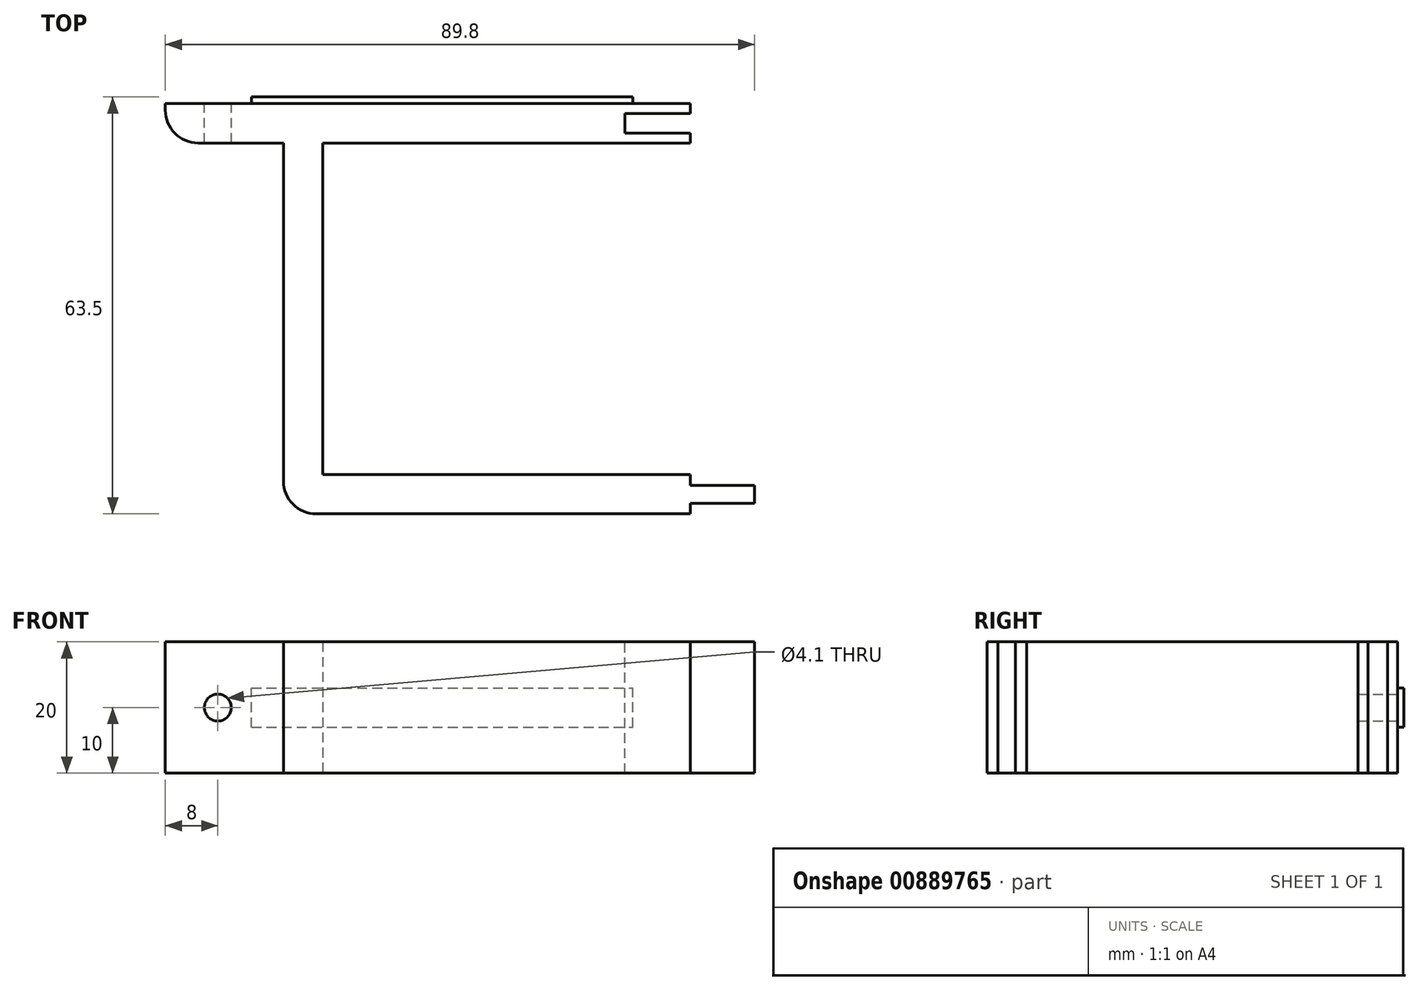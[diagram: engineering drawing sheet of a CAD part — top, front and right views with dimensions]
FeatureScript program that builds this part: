
annotation { "Feature Type Name" : "Feature", "Feature Type Description" : "" }
export const myFeature = defineFeature(function(context is Context, id is Id, definition is map)
    precondition{}
    {
        {
            var Q0;
            Q0=qCreatedBy(makeId("Top.planeOp"),FACE);
            var sketch = newSketch(context, id + "F0", { "sketchPlane" : qUnion([Q0])});
            skLineSegment(sketch, "E0.bottom", {"start": v(-80, 3) * mm, "end": v(80, 3) * mm});
            skLineSegment(sketch, "E0.top", {"start": v(-80, -3) * mm, "end": v(-62, -3) * mm});
            skLineSegment(sketch, "E0.left", {"start": v(-80, 3) * mm, "end": v(-80, -3) * mm});
            skLineSegment(sketch, "E0.right", {"start": v(80, 3) * mm, "end": v(80, -3) * mm});
            skPoint(sketch, "E0.middle", {"position": v(0, 0) * mm});
            skLineSegment(sketch, "E1.bottom", {"start": v(-56, -3) * mm, "end": v(56, -3) * mm});
            skLineSegment(sketch, "E1.top", {"start": v(-56, -53.5) * mm, "end": v(56, -53.5) * mm});
            skLineSegment(sketch, "E1.left", {"start": v(-56, -3) * mm, "end": v(-56, -53.5) * mm});
            skLineSegment(sketch, "E1.right", {"start": v(56, -3) * mm, "end": v(56, -53.5) * mm});
            skLineSegment(sketch, "E2", {"start": v(-62, -3) * mm, "end": v(-62, -59.5) * mm});
            skLineSegment(sketch, "E3", {"start": v(-62, -59.5) * mm, "end": v(62, -59.5) * mm});
            skLineSegment(sketch, "E4", {"start": v(62, -59.5) * mm, "end": v(62, -3) * mm});
            skLineSegment(sketch, "E5.trimOffspring", {"start": v(62, -3) * mm, "end": v(80, -3) * mm});
            skSolve(sketch);
        }
        {
            var Q0;
            Q0=makeQuery(id+"F0.imprint","IMPRINT",FACE,{"disambiguationData":[TD([[makeQuery(id+"F0.imprint","IMPRINT",EDGE,{"derivedFrom":sQuery(id+"F0.wireOp",EDGE,"E0.bottom")}),-1.0]])]});
            extrude(context, id + "F1", {"entities" : qUnion([Q0]), "depth" : 20 * mm, "offsetDistance" : 25 * mm});
        }
        {
            var Q0;
            Q0=makeQuery(id+"F1.opExtrude","SWEPT_EDGE",EDGE,{"disambiguationData":[OSD([sQuery(id+"F0.wireOp",EDGE,"E3"),sQuery(id+"F0.wireOp",EDGE,"E4")])]});
            var Q1;
            Q1=makeQuery(id+"F1.opExtrude","SWEPT_EDGE",EDGE,{"disambiguationData":[OSD([sQuery(id+"F0.wireOp",EDGE,"E2"),sQuery(id+"F0.wireOp",EDGE,"E3")])]});
            var Q2;
            Q2=makeQuery(id+"F1.opExtrude","SWEPT_EDGE",EDGE,{"disambiguationData":[OSD([sQuery(id+"F0.wireOp",EDGE,"E0.top"),sQuery(id+"F0.wireOp",EDGE,"E0.left")])]});
            var Q3;
            Q3=makeQuery(id+"F1.opExtrude","SWEPT_EDGE",EDGE,{"disambiguationData":[OSD([sQuery(id+"F0.wireOp",EDGE,"E0.right"),sQuery(id+"F0.wireOp",EDGE,"E5.trimOffspring")])]});
            fillet(context, id + "F2", {"entities" : qUnion([Q0, Q1, Q2, Q3]), "radius" : 5 * mm, "tangentPropagation" : true, "allowEdgeOverflow" : false});
        }
        {
            var Q0;
            Q0=makeQuery(id+"F1.opExtrude","SWEPT_FACE",FACE,{"disambiguationData":[OSD([sQuery(id+"F0.wireOp",EDGE,"E0.bottom")])]});
            var sketch = newSketch(context, id + "F3", { "sketchPlane" : qUnion([Q0])});
            skPoint(sketch, "E6", {"position": v(-72, 10) * mm});
            skPoint(sketch, "E7", {"position": v(72, 10) * mm});
            skSolve(sketch);
        }
        {
            var Q0;
            Q0=sQuery(id+"F3.wireOp",VERTEX,"E6");
            var Q1;
            Q1=sQuery(id+"F3.wireOp",VERTEX,"E7");
            var Q2;
            Q2=makeQuery(id+"F1.opExtrude","SWEPT_BODY",BODY,{"disambiguationData":[OSD([sQuery(id+"F0.wireOp",EDGE,"E0.bottom"),sQuery(id+"F0.wireOp",EDGE,"E0.top"),sQuery(id+"F0.wireOp",EDGE,"E0.left"),sQuery(id+"F0.wireOp",EDGE,"E0.right"),sQuery(id+"F0.wireOp",EDGE,"E1.top"),sQuery(id+"F0.wireOp",EDGE,"E1.left"),sQuery(id+"F0.wireOp",EDGE,"E1.right"),sQuery(id+"F0.wireOp",EDGE,"E2"),sQuery(id+"F0.wireOp",EDGE,"E3"),sQuery(id+"F0.wireOp",EDGE,"E4"),sQuery(id+"F0.wireOp",EDGE,"E5.trimOffspring"),sQuery(id+"F0.wireOp",EDGE,"E1.bottom")])]});
            hole(context, id + "F4", {"style" : HoleStyle.SIMPLE, "endStyle" : HoleEndStyle.THROUGH, "holeDiameter" : 4.1 * mm, "majorDiameter" : 5 * mm, "isTappedThrough" : true, "tappedDepth" : 12 * mm, "tapClearance" : 3, "locations" : qUnion([Q0, Q1]), "scope" : qUnion([Q2])});
        }
        {
            var Q0;
            Q0=makeQuery(id+"F1.opExtrude","CAP_FACE",FACE,{"disambiguationData":[OSD([sQuery(id+"F0.wireOp",EDGE,"E0.bottom"),sQuery(id+"F0.wireOp",EDGE,"E0.top"),sQuery(id+"F0.wireOp",EDGE,"E0.left"),sQuery(id+"F0.wireOp",EDGE,"E0.right"),sQuery(id+"F0.wireOp",EDGE,"E1.top"),sQuery(id+"F0.wireOp",EDGE,"E1.left"),sQuery(id+"F0.wireOp",EDGE,"E1.right"),sQuery(id+"F0.wireOp",EDGE,"E2"),sQuery(id+"F0.wireOp",EDGE,"E3"),sQuery(id+"F0.wireOp",EDGE,"E4"),sQuery(id+"F0.wireOp",EDGE,"E5.trimOffspring"),sQuery(id+"F0.wireOp",EDGE,"E1.bottom")])],"isStart":false});
            var sketch = newSketch(context, id + "F5", { "sketchPlane" : qUnion([Q0])});
            skLineSegment(sketch, "E8.bottom", {"start": v(9.8, -55.18) * mm, "end": v(0, -55.18) * mm});
            skLineSegment(sketch, "E8.top", {"start": v(9.8, -57.88) * mm, "end": v(0, -57.88) * mm});
            skLineSegment(sketch, "E8.left", {"start": v(9.8, -55.18) * mm, "end": v(9.8, -57.88) * mm});
            skPoint(sketch, "E8.middle.positionSnap0", {"position": v(0, -53.5) * mm});
            skPoint(sketch, "E8.centerSnap0", {"position": v(0, -53.5) * mm});
            skLineSegment(sketch, "E9.bottom", {"start": v(0, 1.5) * mm, "end": v(-10, 1.5) * mm});
            skLineSegment(sketch, "E9.top", {"start": v(0, -1.5) * mm, "end": v(-10, -1.5) * mm});
            skLineSegment(sketch, "E9.right", {"start": v(-10, 1.5) * mm, "end": v(-10, -1.5) * mm});
            skPoint(sketch, "E9.middle", {"position": v(0, 0) * mm});
            skLineSegment(sketch, "E10", {"start": v(0, -55.18) * mm, "end": v(0, -53.5) * mm});
            skLineSegment(sketch, "E11", {"start": v(0, -57.88) * mm, "end": v(0, -59.5) * mm});
            skLineSegment(sketch, "E12", {"start": v(0, -3) * mm, "end": v(0, -1.5) * mm});
            skLineSegment(sketch, "E13", {"start": v(0, 3) * mm, "end": v(0, 1.5) * mm});
            skSolve(sketch);
        }
        {
            var Q0;
            Q0=makeQuery(id+"F5.imprint","IMPRINT",FACE,{"disambiguationData":[TD([[makeQuery(id+"F5.imprint","IMPRINT",EDGE,{"derivedFrom":sQuery(id+"F5.wireOp",EDGE,"E8.bottom")}),-1.0]])]});
            extrude(context, id + "F6", {"entities" : qUnion([Q0]), "operationType" : NewBodyOperationType.REMOVE, "endBound" : BoundingType.UP_TO_NEXT, "oppositeDirection" : true, "depth" : 25 * mm, "offsetDistance" : 25 * mm});
        }
        {
            var Q0;
            Q0=makeQuery(id+"F1.opExtrude","SWEPT_FACE",FACE,{"disambiguationData":[OSD([sQuery(id+"F0.wireOp",EDGE,"E0.bottom")])]});
            var sketch = newSketch(context, id + "F7", { "sketchPlane" : qUnion([Q0])});
            skLineSegment(sketch, "E14.bottom", {"start": v(66.87, 7) * mm, "end": v(8.74, 7) * mm});
            skLineSegment(sketch, "E14.top", {"start": v(66.87, 13) * mm, "end": v(8.74, 13) * mm});
            skLineSegment(sketch, "E14.left", {"start": v(66.87, 7) * mm, "end": v(66.87, 13) * mm});
            skPoint(sketch, "E14.middle", {"position": v(0, 10) * mm});
            skLineSegment(sketch, "E15", {"start": v(8.74, 7) * mm, "end": v(8.74, 13) * mm});
            skSolve(sketch);
        }
        {
            var Q0;
            Q0=makeQuery(id+"F7.imprint","IMPRINT",FACE,{"disambiguationData":[TD([[makeQuery(id+"F7.imprint","IMPRINT",EDGE,{"derivedFrom":sQuery(id+"F7.wireOp",EDGE,"E14.bottom")}),-1.0]])]});
            extrude(context, id + "F8", {"entities" : qUnion([Q0]), "operationType" : NewBodyOperationType.ADD, "depth" : 1 * mm, "offsetDistance" : 25 * mm});
        }
    });
